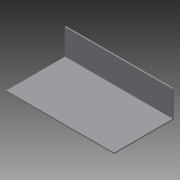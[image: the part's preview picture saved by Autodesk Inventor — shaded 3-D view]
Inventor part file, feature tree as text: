
AUTODESK INVENTOR PART (.ipt)
format: ipt  version: 2015 (Build 190159000, 159)  size: 86,016 bytes
history: native  units: mm
features: extrude x2, sketch x2, fillet x1
ambient origin geometry x8: Origin, YZ Plane, XZ Plane, XY Plane, X Axis, Y Axis, Z Axis, Center Point
bodies: Body1 (feature_tree)
feature tree (5):
  extrude  "Extrusion2"  Depth=110.0mm
  extrude  "Extrusion3"  Depth=2.0mm
  fillet  "Fillet1"  Radius=48.0mm
  sketch  "Sketch2"  dims[d4=199.0mm d5=110.0mm]
  sketch  "Sketch3"  dims[d6=2.0mm d7=0.0mm d8=2.0mm d9=48.0mm d10=0.0mm d11=1.0mm]
